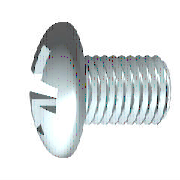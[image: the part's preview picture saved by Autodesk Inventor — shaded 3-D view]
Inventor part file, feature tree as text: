
AUTODESK INVENTOR PART (.ipt)
format: ipt  version: 2013 (Build 170138000, 138)  size: 259,072 bytes
history: native  units: mm (DEFAULTED — no unit token found)
features: extrude x1, other x1, plane x1
ambient origin geometry x7: Origin, YZ Plane, XZ Plane, X Axis, Y Axis, Z Axis, Center Point
bodies: Solid1 (feature_tree), Body (feature_tree)
feature tree (3):
  extrude  "Slot"  Depth=4.1656mm
  other  "Cut"
  plane  "Work Plane3"
